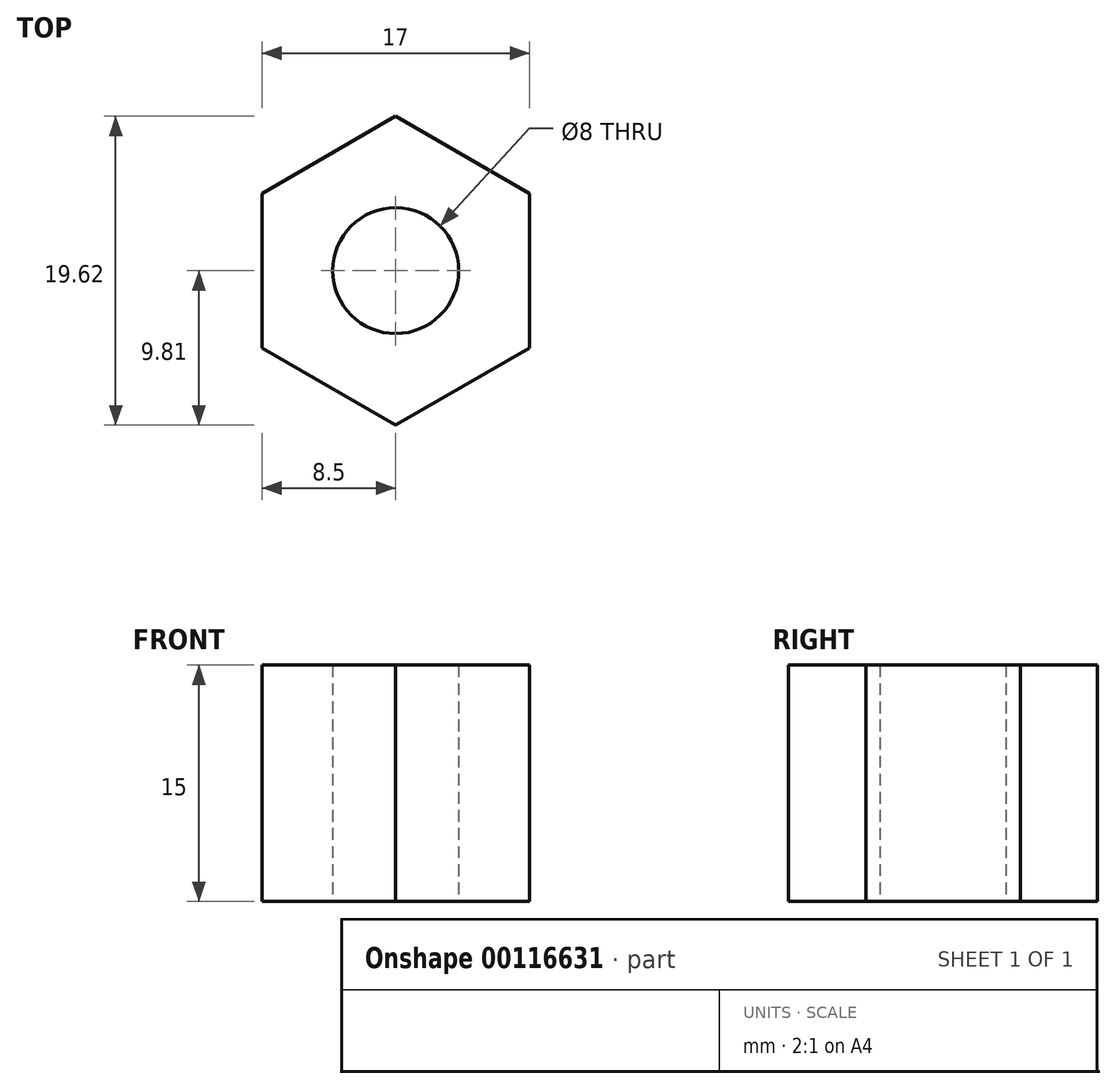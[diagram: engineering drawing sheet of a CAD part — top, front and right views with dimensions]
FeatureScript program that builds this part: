
annotation { "Feature Type Name" : "Feature", "Feature Type Description" : "" }
export const myFeature = defineFeature(function(context is Context, id is Id, definition is map)
    precondition{}
    {
        {
            var Q0;
            Q0=qCreatedBy(makeId("Top.planeOp"),FACE);
            var sketch = newSketch(context, id + "F0", { "sketchPlane" : qUnion([Q0])});
            skCircle(sketch, "E0.cCircle", {"center": v(0, 0) * mm, "radius": 8.5 * mm, "construction": true});
            skLineSegment(sketch, "E0.0", {"start": v(8.5, -4.9) * mm, "end": v(0, -9.81) * mm});
            skLineSegment(sketch, "E0.1", {"start": v(0, -9.81) * mm, "end": v(-8.5, -4.9) * mm});
            skLineSegment(sketch, "E0.2", {"start": v(-8.5, -4.9) * mm, "end": v(-8.5, 4.9) * mm});
            skLineSegment(sketch, "E0.3", {"start": v(-8.5, 4.9) * mm, "end": v(0, 9.81) * mm});
            skLineSegment(sketch, "E0.4", {"start": v(0, 9.81) * mm, "end": v(8.5, 4.9) * mm});
            skLineSegment(sketch, "E0.5", {"start": v(8.5, 4.9) * mm, "end": v(8.5, -4.9) * mm});
            skPoint(sketch, "E0.0.midPoint", {"position": v(4.25, -7.36) * mm});
            skCircle(sketch, "E1", {"center": v(0, 0) * mm, "radius": 4 * mm});
            skSolve(sketch);
        }
        {
            var Q0;
            Q0 = qSketchRegion(id + "F0", true);
            extrude(context, id + "F1", {"entities" : qUnion([Q0]), "endBound" : BoundingType.SYMMETRIC, "depth" : 15 * mm});
        }
        {
            var Q0;
            Q0=makeQuery(id+"F1.opExtrude","SWEPT_BODY",BODY,{"disambiguationData":[OSD([sQuery(id+"F0.wireOp",EDGE,"E0.0"),sQuery(id+"F0.wireOp",EDGE,"E0.1"),sQuery(id+"F0.wireOp",EDGE,"E0.2"),sQuery(id+"F0.wireOp",EDGE,"E0.3"),sQuery(id+"F0.wireOp",EDGE,"E0.4"),sQuery(id+"F0.wireOp",EDGE,"E0.5"),sQuery(id+"F0.wireOp",EDGE,"E1")])]});
            transform(context, id + "F2", {"entities" : qUnion([Q0]), "transformType" : TransformType.TRANSLATION_3D, "dx" : 50 * mm, "dy" : 50 * mm, "dz" : 0 * mm, "makeCopy" : false});
        }
    });
